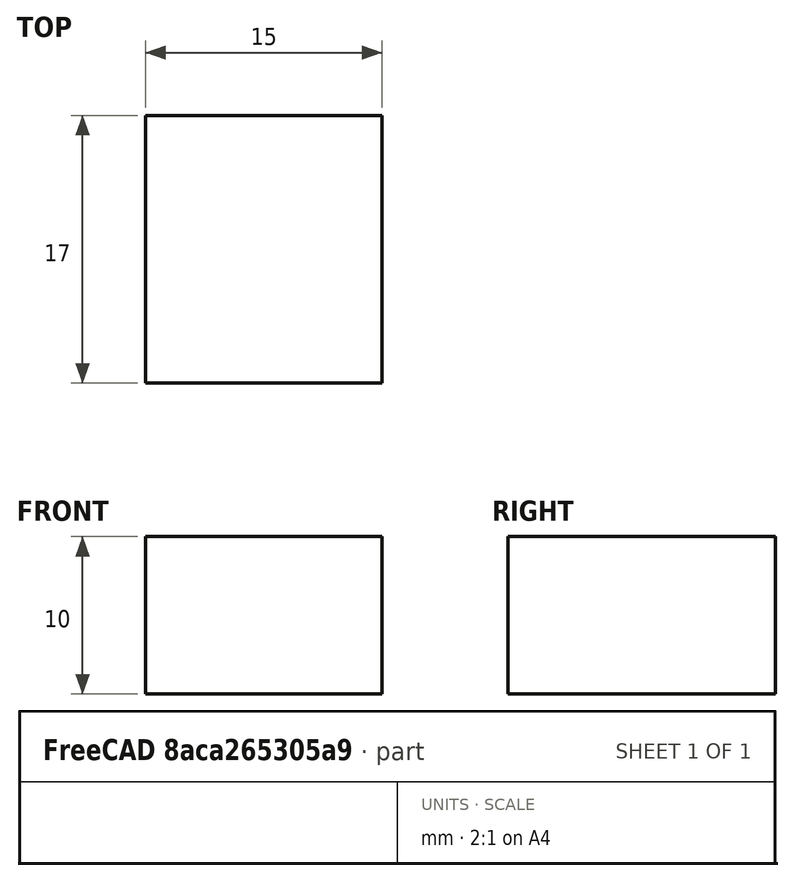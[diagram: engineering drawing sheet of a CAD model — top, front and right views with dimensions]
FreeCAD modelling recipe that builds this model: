
FCSTD DOCUMENT  (FreeCAD 0.15R4671 (Git))
Label: flexure_stage_1
License: All rights reserved
LicenseURL: http://en.wikipedia.org/wiki/All_rights_reserved
objects: Sketcher::SketchObject×1, PartDesign::Pad×1
note: 3 computed .brp shape members not serialized (recipe doc carries the construction recipe); baked Part::Feature solids carry a one-line shape summary decoded from their .brp

FEATURE [Sketcher::SketchObject] Sketch
  sketch-geometry (4):
    g0: LineSegment StartX=-7.5 StartY=-8.5 StartZ=0 EndX=7.5 EndY=-8.5 EndZ=0
    g1: LineSegment StartX=7.5 StartY=-8.5 StartZ=0 EndX=7.5 EndY=8.5 EndZ=0
    g2: LineSegment StartX=7.5 StartY=8.5 StartZ=0 EndX=-7.5 EndY=8.5 EndZ=0
    g3: LineSegment StartX=-7.5 StartY=8.5 StartZ=0 EndX=-7.5 EndY=-8.5 EndZ=0
  constraints (8):
    c: Coincident(g0,g1)
    c: Coincident(g1,g2)
    c: Coincident(g2,g3)
    c: Coincident(g3,g0)
    c: Horizontal(g0)
    c: Horizontal(g2)
    c: Vertical(g1)
    c: Vertical(g3)
FEATURE [PartDesign::Pad] Pad
  Length = 10
  Length2 = 100
  Sketch = -> Sketch
  Type = 0
